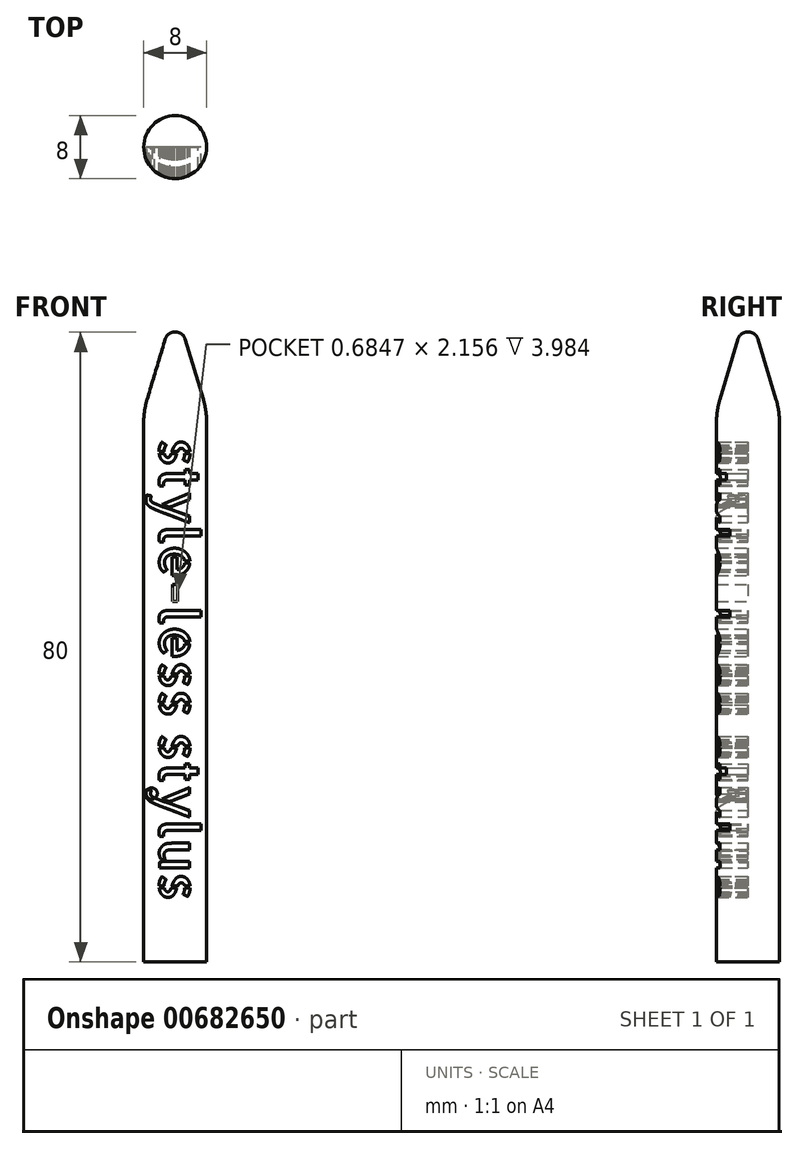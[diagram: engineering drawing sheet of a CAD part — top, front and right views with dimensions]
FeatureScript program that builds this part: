
annotation { "Feature Type Name" : "Feature", "Feature Type Description" : "" }
export const myFeature = defineFeature(function(context is Context, id is Id, definition is map)
    precondition{}
    {
        {
            var Q0;
            Q0=qCreatedBy(makeId("Front.planeOp"),FACE);
            var sketch = newSketch(context, id + "F0", { "sketchPlane" : qUnion([Q0])});
            skPoint(sketch, "E0.middle", {"position": v(0, 0) * mm});
            skLineSegment(sketch, "E1", {"start": v(0, 0) * mm, "end": v(0, 80) * mm});
            skLineSegment(sketch, "E2", {"start": v(0, 80) * mm, "end": v(4, 80) * mm});
            skLineSegment(sketch, "E3", {"start": v(4, 80) * mm, "end": v(4, 0) * mm});
            skLineSegment(sketch, "E4", {"start": v(4, 0) * mm, "end": v(0, 0) * mm});
            skSolve(sketch);
        }
        {
            var Q0;
            Q0=makeQuery(id+"F0.imprint","IMPRINT",FACE,{"disambiguationData":[TD([[makeQuery(id+"F0.imprint","IMPRINT",EDGE,{"derivedFrom":sQuery(id+"F0.wireOp",EDGE,"E1")}),-1.0]])]});
            var Q1;
            Q1=sQuery(id+"F0.wireOp",EDGE,"E1");
            revolve(context, id + "F1", {"entities" : qUnion([Q0]), "axis" : qUnion([Q1]), "revolveType" : RevolveType.FULL});
        }
        {
            var Q0;
            Q0=makeQuery(id+"F1.opRevolve","SWEPT_EDGE",EDGE,{"disambiguationData":[OSD([sQuery(id+"F0.wireOp",EDGE,"E2"),sQuery(id+"F0.wireOp",EDGE,"E3")])]});
            chamfer(context, id + "F2", {"entities" : qUnion([Q0]), "chamferType" : ChamferType.TWO_OFFSETS, "width1" : 10 * mm, "oppositeDirection" : false, "width2" : 3 * mm, "tangentPropagation" : true});
        }
        {
            var Q0;
            {var subQ0=sQuery(id+"F0.wireOp",EDGE,"E2");Q0=makeQuery(id+"F2.opChamfer","BLEND_EDGE",EDGE,{"blendedFrom":[makeQuery(id+"F1.opRevolve","SWEPT_EDGE",EDGE,{"disambiguationData":[OSD([subQ0,sQuery(id+"F0.wireOp",EDGE,"E3")])]}),makeQuery(id+"F1.opRevolve","SWEPT_FACE",FACE,{"disambiguationData":[OSD([subQ0])]})],"blendedInto":[makeQuery(id+"F1.opRevolve","SWEPT_FACE",FACE,{"disambiguationData":[OSD([subQ0])]})]});}
            fillet(context, id + "F3", {"entities" : qUnion([Q0]), "radius" : 1.2 * mm, "tangentPropagation" : true, "allowEdgeOverflow" : false});
        }
        {
            var Q0;
            {var subQ0=sQuery(id+"F0.wireOp",EDGE,"E3");Q0=makeQuery(id+"F2.opChamfer","BLEND_EDGE",EDGE,{"blendedFrom":[makeQuery(id+"F1.opRevolve","SWEPT_EDGE",EDGE,{"disambiguationData":[OSD([sQuery(id+"F0.wireOp",EDGE,"E2"),subQ0])]}),makeQuery(id+"F1.opRevolve","SWEPT_FACE",FACE,{"disambiguationData":[OSD([subQ0])]})],"blendedInto":[makeQuery(id+"F1.opRevolve","SWEPT_FACE",FACE,{"disambiguationData":[OSD([subQ0])]})]});}
            fillet(context, id + "F4", {"entities" : qUnion([Q0]), "radius" : 10 * mm, "tangentPropagation" : true, "allowEdgeOverflow" : false});
        }
        {
            var Q0;
            Q0=qCreatedBy(makeId("Front.planeOp"),FACE);
            var sketch = newSketch(context, id + "F5", { "sketchPlane" : qUnion([Q0])});
            skText(sketch, "E5", { "text": "style-less stylus", "fontName": "AllertaStencil-Regular.ttf"});
            const initialGuessF5  = {"E5": [-0.002, 0.06653, 0, -1, 0.005]};
            skSetInitialGuess(sketch, initialGuessF5);
            skSolve(sketch);
        }
        {
            var Q0;
            Q0 = qSketchRegion(id + "F5", true);
            extrude(context, id + "F6", {"entities" : qUnion([Q0]), "operationType" : NewBodyOperationType.REMOVE, "oppositeDirection" : true, "depth" : -10 * mm, "offsetDistance" : 25 * mm});
        }
    });
